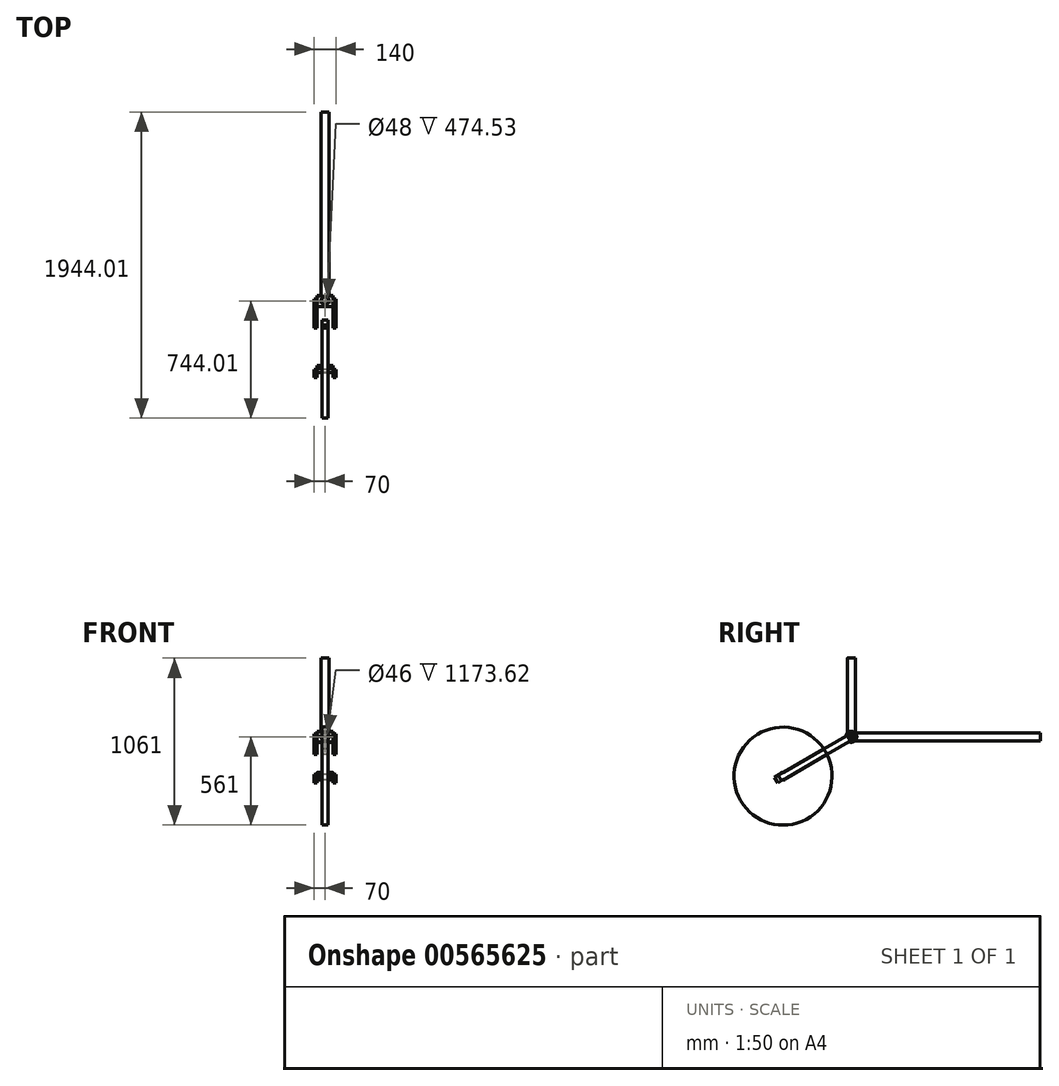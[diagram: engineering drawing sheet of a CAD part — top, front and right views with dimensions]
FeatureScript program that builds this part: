
annotation { "Feature Type Name" : "Feature", "Feature Type Description" : "" }
export const myFeature = defineFeature(function(context is Context, id is Id, definition is map)
    precondition{}
    {
        {
            var Q0;
            Q0=qCreatedBy(makeId("Right.planeOp"),FACE);
            var sketch = newSketch(context, id + "F0", { "sketchPlane" : qUnion([Q0])});
            skCircle(sketch, "E0", {"center": v(0, 0) * mm, "radius": 20 * mm});
            skCircle(sketch, "E1", {"center": v(0, 0) * mm, "radius": 35 * mm});
            skLineSegment(sketch, "E2", {"start": v(0, 0) * mm, "end": v(0, 136.2) * mm, "construction": true});
            skLineSegment(sketch, "E3", {"start": v(0, 0) * mm, "end": v(-10, 17.32) * mm, "construction": true});
            skLineSegment(sketch, "E4", {"start": v(0, 0) * mm, "end": v(-17.5, 30.31) * mm, "construction": true});
            skLineSegment(sketch, "E5", {"start": v(0, 0) * mm, "end": v(-433.01, -250) * mm, "construction": true});
            skLineSegment(sketch, "E6", {"start": v(0, 0) * mm, "end": v(-10, 17.32) * mm});
            skLineSegment(sketch, "E7", {"start": v(-10, 17.32) * mm, "end": v(-486.31, -257.68) * mm});
            skLineSegment(sketch, "E8", {"start": v(-486.31, -257.68) * mm, "end": v(-466.31, -292.32) * mm});
            skLineSegment(sketch, "E9", {"start": v(-466.31, -292.32) * mm, "end": v(10, -17.32) * mm});
            skLineSegment(sketch, "E10", {"start": v(10, -17.32) * mm, "end": v(0, 0) * mm});
            skCircle(sketch, "E11", {"center": v(-433.01, -250) * mm, "radius": 25 * mm});
            skCircle(sketch, "E12", {"center": v(-433.01, -250) * mm, "radius": 311 * mm});
            skSolve(sketch);
        }
        {
            var Q0;
            Q0=makeQuery(id+"F0.imprint","IMPRINT",FACE,{"disambiguationData":[TD([[makeQuery(id+"F0.imprint","IMPRINT",EDGE,{"derivedFrom":sQuery(id+"F0.wireOp",EDGE,"E0")}),-1.0]])]});
            var Q1;
            {var subQ0=sQuery(id+"F0.wireOp",EDGE,"E7");var subQ5=sQuery(id+"F0.wireOp",EDGE,"E1");var subQ6=makeQuery(id+"F0.imprint","INTERSECT",VERTEX,{"derivedFrom":[subQ5,subQ0]});Q1=makeQuery(id+"F0.imprint","IMPRINT",FACE,{"disambiguationData":[TD([[makeQuery(id+"F0.imprint","IMPRINT",EDGE,{"disambiguationData":[TD([[subQ6,-1.0]])],"derivedFrom":subQ5}),1.0]])]});}
            extrude(context, id + "F1", {"entities" : qUnion([Q0, Q1]), "endBound" : BoundingType.SYMMETRIC, "depth" : 100 * mm, "offsetDistance" : 25 * mm});
        }
        {
            var Q0;
            Q0=qCreatedBy(makeId("Front.planeOp"),FACE);
            var sketch = newSketch(context, id + "F2", { "sketchPlane" : qUnion([Q0])});
            skCircle(sketch, "E13", {"center": v(0, 0) * mm, "radius": 25 * mm});
            skCircle(sketch, "E14", {"center": v(0, 0) * mm, "radius": 23 * mm});
            skSolve(sketch);
        }
        {
            var Q0;
            Q0 = qSketchRegion(id + "F2", true);
            extrude(context, id + "F3", {"entities" : qUnion([Q0]), "operationType" : NewBodyOperationType.ADD, "oppositeDirection" : true, "depth" : 1200 * mm, "offsetDistance" : 25 * mm});
        }
        {
            var Q0;
            Q0=qCreatedBy(makeId("Top.planeOp"),FACE);
            var sketch = newSketch(context, id + "F4", { "sketchPlane" : qUnion([Q0])});
            skCircle(sketch, "E15", {"center": v(0, 0) * mm, "radius": 25 * mm});
            skCircle(sketch, "E16", {"center": v(0, 0) * mm, "radius": 24 * mm});
            skSolve(sketch);
        }
        {
            var Q0;
            Q0 = qSketchRegion(id + "F4", true);
            extrude(context, id + "F5", {"entities" : qUnion([Q0]), "operationType" : NewBodyOperationType.ADD, "depth" : 500 * mm, "offsetDistance" : 25 * mm});
        }
        {
            var Q0;
            {var subQ5=sQuery(id+"F0.wireOp",EDGE,"E8");Q0=makeQuery(id+"F0.imprint","IMPRINT",FACE,{"disambiguationData":[TD([[makeQuery(id+"F0.imprint","IMPRINT",EDGE,{"derivedFrom":subQ5}),1.0]])]});}
            var Q1;
            {var subQ1=sQuery(id+"F0.wireOp",EDGE,"E0");var subQ7=makeQuery(id+"F0.imprint","IMPRINT",VERTEX,{"derivedFrom":subQ1});Q1=makeQuery(id+"F0.imprint","IMPRINT",FACE,{"disambiguationData":[TD([[makeQuery(id+"F0.imprint","IMPRINT",EDGE,{"disambiguationData":[TD([[subQ7,1.0]])],"derivedFrom":subQ1}),-1.0]])]});}
            var Q2;
            {var subQ0=sQuery(id+"F0.wireOp",EDGE,"E7");var subQ5=sQuery(id+"F0.wireOp",EDGE,"E1");var subQ6=makeQuery(id+"F0.imprint","INTERSECT",VERTEX,{"derivedFrom":[subQ5,subQ0]});Q2=makeQuery(id+"F0.imprint","IMPRINT",FACE,{"disambiguationData":[TD([[makeQuery(id+"F0.imprint","IMPRINT",EDGE,{"disambiguationData":[TD([[subQ6,-1.0]])],"derivedFrom":subQ5}),1.0]])]});}
            var Q3;
            {var subQ0=sQuery(id+"F0.wireOp",EDGE,"E11");var subQ3=makeQuery(id+"F0.imprint","IMPRINT",VERTEX,{"derivedFrom":subQ0});Q3=makeQuery(id+"F0.imprint","IMPRINT",FACE,{"disambiguationData":[TD([[makeQuery(id+"F0.imprint","IMPRINT",EDGE,{"disambiguationData":[TD([[subQ3,1.0]])],"derivedFrom":subQ0}),1.0]])]});}
            var Q4;
            {var subQ0=sQuery(id+"F0.wireOp",EDGE,"E11");var subQ1=makeQuery(id+"F0.imprint","IMPRINT",VERTEX,{"derivedFrom":subQ0});Q4=makeQuery(id+"F0.imprint","IMPRINT",FACE,{"disambiguationData":[TD([[makeQuery(id+"F0.imprint","IMPRINT",EDGE,{"disambiguationData":[TD([[subQ1,1.0]])],"derivedFrom":subQ0}),-1.0]])]});}
            var Q5;
            {var subQ0=sQuery(id+"F0.wireOp",EDGE,"E7");var subQ1=sQuery(id+"F0.wireOp",EDGE,"E1");var subQ2=makeQuery(id+"F0.imprint","INTERSECT",VERTEX,{"derivedFrom":[subQ1,subQ0]});Q5=makeQuery(id+"F0.imprint","IMPRINT",FACE,{"disambiguationData":[TD([[makeQuery(id+"F0.imprint","IMPRINT",EDGE,{"disambiguationData":[TD([[subQ2,-1.0]])],"derivedFrom":subQ1}),-1.0]])]});}
            extrude(context, id + "F6", {"entities" : qUnion([Q0, Q1, Q2, Q3, Q4, Q5]), "endBound" : BoundingType.SYMMETRIC, "depth" : 140 * mm, "offsetDistance" : 25 * mm});
        }
        {
            var Q0;
            {var subQ5=sQuery(id+"F0.wireOp",EDGE,"E8");Q0=makeQuery(id+"F0.imprint","IMPRINT",FACE,{"disambiguationData":[TD([[makeQuery(id+"F0.imprint","IMPRINT",EDGE,{"derivedFrom":subQ5}),1.0]])]});}
            var Q1;
            {var subQ0=sQuery(id+"F0.wireOp",EDGE,"E7");var subQ5=sQuery(id+"F0.wireOp",EDGE,"E1");var subQ6=makeQuery(id+"F0.imprint","INTERSECT",VERTEX,{"derivedFrom":[subQ5,subQ0]});Q1=makeQuery(id+"F0.imprint","IMPRINT",FACE,{"disambiguationData":[TD([[makeQuery(id+"F0.imprint","IMPRINT",EDGE,{"disambiguationData":[TD([[subQ6,-1.0]])],"derivedFrom":subQ5}),1.0]])]});}
            var Q2;
            {var subQ1=sQuery(id+"F0.wireOp",EDGE,"E0");var subQ7=makeQuery(id+"F0.imprint","IMPRINT",VERTEX,{"derivedFrom":subQ1});Q2=makeQuery(id+"F0.imprint","IMPRINT",FACE,{"disambiguationData":[TD([[makeQuery(id+"F0.imprint","IMPRINT",EDGE,{"disambiguationData":[TD([[subQ7,1.0]])],"derivedFrom":subQ1}),-1.0]])]});}
            var Q3;
            {var subQ0=sQuery(id+"F0.wireOp",EDGE,"E7");var subQ1=sQuery(id+"F0.wireOp",EDGE,"E1");var subQ2=makeQuery(id+"F0.imprint","INTERSECT",VERTEX,{"derivedFrom":[subQ1,subQ0]});Q3=makeQuery(id+"F0.imprint","IMPRINT",FACE,{"disambiguationData":[TD([[makeQuery(id+"F0.imprint","IMPRINT",EDGE,{"disambiguationData":[TD([[subQ2,-1.0]])],"derivedFrom":subQ1}),-1.0]])]});}
            var Q4;
            {var subQ0=sQuery(id+"F0.wireOp",EDGE,"E11");var subQ1=makeQuery(id+"F0.imprint","IMPRINT",VERTEX,{"derivedFrom":subQ0});Q4=makeQuery(id+"F0.imprint","IMPRINT",FACE,{"disambiguationData":[TD([[makeQuery(id+"F0.imprint","IMPRINT",EDGE,{"disambiguationData":[TD([[subQ1,1.0]])],"derivedFrom":subQ0}),-1.0]])]});}
            var Q5;
            {var subQ0=sQuery(id+"F0.wireOp",EDGE,"E11");var subQ3=makeQuery(id+"F0.imprint","IMPRINT",VERTEX,{"derivedFrom":subQ0});Q5=makeQuery(id+"F0.imprint","IMPRINT",FACE,{"disambiguationData":[TD([[makeQuery(id+"F0.imprint","IMPRINT",EDGE,{"disambiguationData":[TD([[subQ3,1.0]])],"derivedFrom":subQ0}),1.0]])]});}
            extrude(context, id + "F7", {"entities" : qUnion([Q0, Q1, Q2, Q3, Q4, Q5]), "operationType" : NewBodyOperationType.REMOVE, "endBound" : BoundingType.SYMMETRIC, "depth" : 100 * mm, "offsetDistance" : 25 * mm});
        }
        {
            var Q0;
            {var subQ0=sQuery(id+"F0.wireOp",EDGE,"E11");var subQ3=makeQuery(id+"F0.imprint","IMPRINT",VERTEX,{"derivedFrom":subQ0});Q0=makeQuery(id+"F0.imprint","IMPRINT",FACE,{"disambiguationData":[TD([[makeQuery(id+"F0.imprint","IMPRINT",EDGE,{"disambiguationData":[TD([[subQ3,1.0]])],"derivedFrom":subQ0}),1.0]])]});}
            var Q1;
            {var subQ0=sQuery(id+"F0.wireOp",EDGE,"E11");var subQ1=sQuery(id+"F0.wireOp",EDGE,"E7");var subQ2=makeQuery(id+"F0.imprint","INTERSECT",VERTEX,{"disambiguationData":[OD(0.0)],"derivedFrom":[subQ1,subQ0]});Q1=makeQuery(id+"F0.imprint","IMPRINT",FACE,{"disambiguationData":[TD([[makeQuery(id+"F0.imprint","IMPRINT",EDGE,{"disambiguationData":[TD([[subQ2,-1.0]])],"derivedFrom":subQ1}),-1.0]])]});}
            var Q2;
            {var subQ0=sQuery(id+"F0.wireOp",EDGE,"E11");var subQ1=sQuery(id+"F0.wireOp",EDGE,"E9");var subQ2=makeQuery(id+"F0.imprint","INTERSECT",VERTEX,{"disambiguationData":[OD(0.0)],"derivedFrom":[subQ1,subQ0]});Q2=makeQuery(id+"F0.imprint","IMPRINT",FACE,{"disambiguationData":[TD([[makeQuery(id+"F0.imprint","IMPRINT",EDGE,{"disambiguationData":[TD([[subQ2,1.0]])],"derivedFrom":subQ1}),-1.0]])]});}
            extrude(context, id + "F8", {"entities" : qUnion([Q0, Q1, Q2]), "endBound" : BoundingType.SYMMETRIC, "depth" : 100 * mm, "offsetDistance" : 25 * mm});
        }
        {
            var Q0;
            {var subQ5=sQuery(id+"F0.wireOp",EDGE,"E8");Q0=makeQuery(id+"F0.imprint","IMPRINT",FACE,{"disambiguationData":[TD([[makeQuery(id+"F0.imprint","IMPRINT",EDGE,{"derivedFrom":subQ5}),-1.0]])]});}
            var Q1;
            {var subQ0=sQuery(id+"F0.wireOp",EDGE,"E11");var subQ1=makeQuery(id+"F0.imprint","IMPRINT",VERTEX,{"derivedFrom":subQ0});Q1=makeQuery(id+"F0.imprint","IMPRINT",FACE,{"disambiguationData":[TD([[makeQuery(id+"F0.imprint","IMPRINT",EDGE,{"disambiguationData":[TD([[subQ1,1.0]])],"derivedFrom":subQ0}),-1.0]])]});}
            var Q2;
            {var subQ0=sQuery(id+"F0.wireOp",EDGE,"E8");Q2=makeQuery(id+"F0.imprint","IMPRINT",FACE,{"disambiguationData":[TD([[makeQuery(id+"F0.imprint","IMPRINT",EDGE,{"derivedFrom":subQ0}),1.0]])]});}
            extrude(context, id + "F9", {"entities" : qUnion([Q0, Q1, Q2]), "operationType" : NewBodyOperationType.ADD, "endBound" : BoundingType.SYMMETRIC, "depth" : 40 * mm, "offsetDistance" : 25 * mm});
        }
    });
